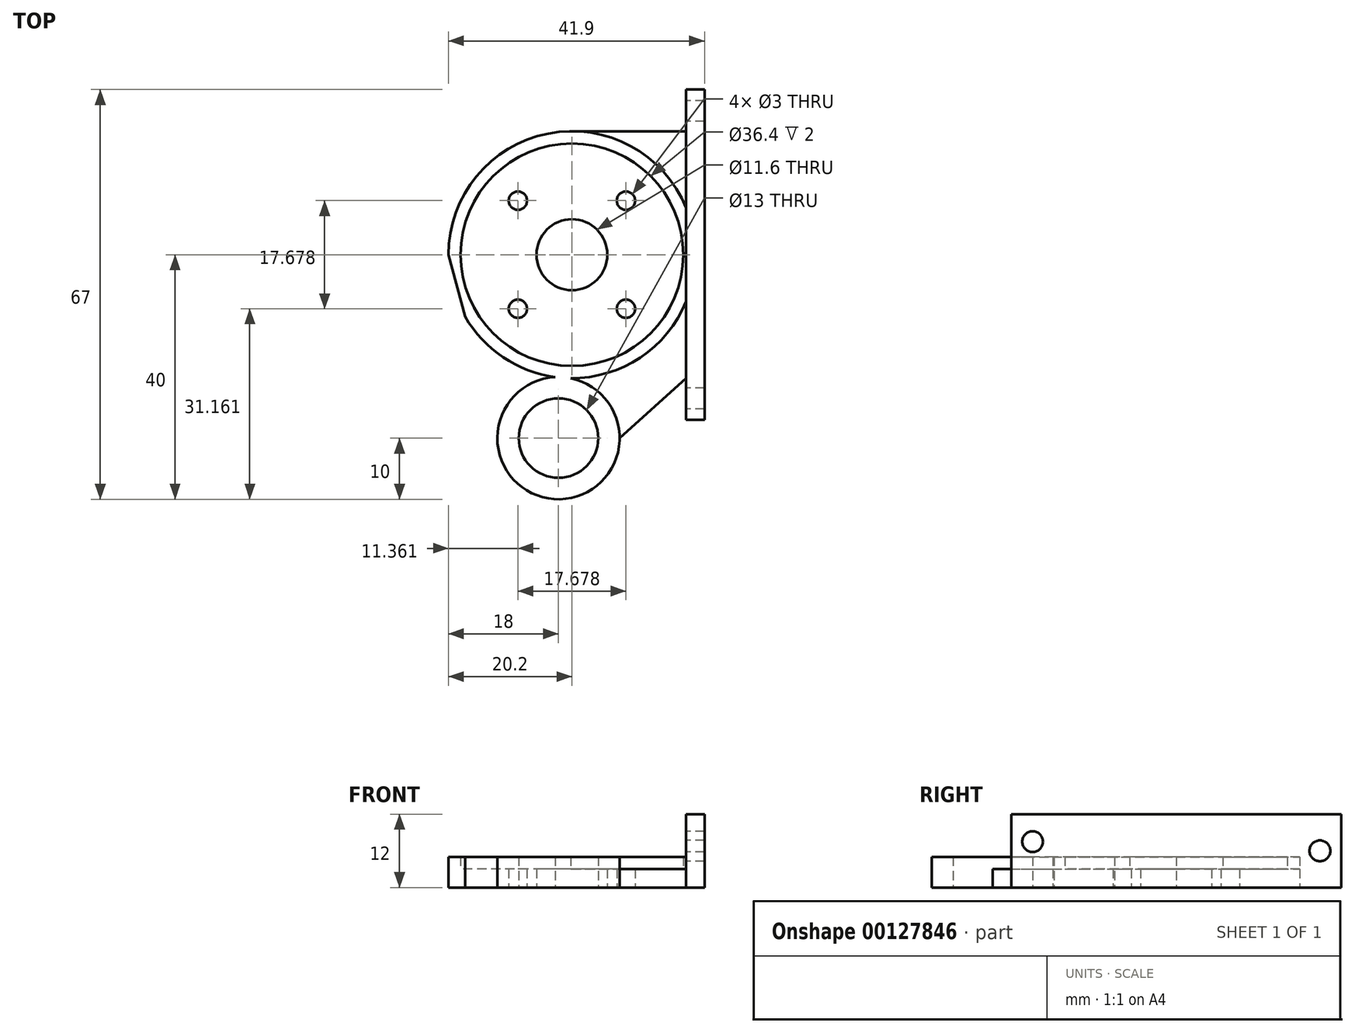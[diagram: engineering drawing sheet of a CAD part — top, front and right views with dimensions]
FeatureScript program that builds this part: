
annotation { "Feature Type Name" : "Feature", "Feature Type Description" : "" }
export const myFeature = defineFeature(function(context is Context, id is Id, definition is map)
    precondition{}
    {
        {
            var Q0;
            Q0=qCreatedBy(makeId("Top.planeOp"),FACE);
            var sketch = newSketch(context, id + "F0", { "sketchPlane" : qUnion([Q0])});
            skCircle(sketch, "E0", {"center": v(0, 0) * mm, "radius": 20.2 * mm});
            skLineSegment(sketch, "E1.bottom", {"start": v(0, 20.2) * mm, "end": v(21.7, 20.2) * mm});
            skLineSegment(sketch, "E1.top", {"start": v(0, -20.2) * mm, "end": v(21.7, -20.2) * mm});
            skLineSegment(sketch, "E1.left", {"start": v(0, 20.2) * mm, "end": v(0, -20.2) * mm});
            skLineSegment(sketch, "E1.right", {"start": v(21.7, 20.2) * mm, "end": v(21.7, -20.2) * mm});
            skLineSegment(sketch, "E2.bottom", {"start": v(21.7, 27) * mm, "end": v(18.7, 27) * mm});
            skLineSegment(sketch, "E2.top", {"start": v(21.7, 0) * mm, "end": v(18.7, 0) * mm});
            skLineSegment(sketch, "E2.left", {"start": v(21.7, 27) * mm, "end": v(21.7, 0) * mm});
            skLineSegment(sketch, "E2.right", {"start": v(18.7, 27) * mm, "end": v(18.7, 0) * mm});
            skLineSegment(sketch, "E3.MirrorCS", {"start": v(21.7, -27) * mm, "end": v(18.7, -27) * mm});
            skLineSegment(sketch, "E4.MirrorCS", {"start": v(18.7, -27) * mm, "end": v(18.7, 0) * mm});
            skLineSegment(sketch, "E5.MirrorCS", {"start": v(21.7, -27) * mm, "end": v(21.7, 0) * mm});
            skCircle(sketch, "E6", {"center": v(0, 0) * mm, "radius": 18.2 * mm});
            skCircle(sketch, "E7.cCircle", {"center": v(0, 0) * mm, "radius": 12.5 * mm, "construction": true});
            skLineSegment(sketch, "E7.0", {"start": v(-8.84, 8.84) * mm, "end": v(8.84, 8.84) * mm});
            skLineSegment(sketch, "E7.1", {"start": v(8.84, 8.84) * mm, "end": v(8.84, -8.84) * mm});
            skLineSegment(sketch, "E7.2", {"start": v(8.84, -8.84) * mm, "end": v(-8.84, -8.84) * mm});
            skLineSegment(sketch, "E7.3", {"start": v(-8.84, -8.84) * mm, "end": v(-8.84, 8.84) * mm});
            skCircle(sketch, "E8", {"center": v(-8.84, -8.84) * mm, "radius": 1.5 * mm});
            skCircle(sketch, "E9", {"center": v(8.84, -8.84) * mm, "radius": 1.5 * mm});
            skCircle(sketch, "E10", {"center": v(8.84, 8.84) * mm, "radius": 1.5 * mm});
            skCircle(sketch, "E11", {"center": v(-8.84, 8.84) * mm, "radius": 1.5 * mm});
            skPoint(sketch, "E12", {"position": v(0, -30) * mm});
            skPoint(sketch, "E13", {"position": v(21.7, -30) * mm});
            skLineSegment(sketch, "E14", {"start": v(21.7, -30) * mm, "end": v(-2.2, -30) * mm});
            skCircle(sketch, "E15", {"center": v(-2.2, -30) * mm, "radius": 6.5 * mm});
            skCircle(sketch, "E16", {"center": v(-2.2, -30) * mm, "radius": 10 * mm});
            skLineSegment(sketch, "E17", {"start": v(-20.2, 0) * mm, "end": v(-12.2, -29.82) * mm});
            skPoint(sketch, "E17.startSnap0", {"position": v(-8.84, 0) * mm});
            skLineSegment(sketch, "E18", {"start": v(7.8, -30) * mm, "end": v(18.7, -20.2) * mm});
            skCircle(sketch, "E19", {"center": v(0, 0) * mm, "radius": 5.8 * mm});
            skSolve(sketch);
        }
        {
            var Q0;
            {var subQ5=sQuery(id+"F0.wireOp",EDGE,"E2.bottom");Q0=makeQuery(id+"F0.imprint","IMPRINT",FACE,{"disambiguationData":[TD([[makeQuery(id+"F0.imprint","IMPRINT",EDGE,{"derivedFrom":subQ5}),1.0]])]});}
            var Q1;
            {var subQ5=sQuery(id+"F0.wireOp",EDGE,"E0");var subQ7=sQuery(id+"F0.wireOp",EDGE,"E2.right");var subQ9=makeQuery(id+"F0.imprint","INTERSECT",VERTEX,{"derivedFrom":[subQ5,subQ7]});Q1=makeQuery(id+"F0.imprint","IMPRINT",FACE,{"disambiguationData":[TD([[makeQuery(id+"F0.imprint","IMPRINT",EDGE,{"disambiguationData":[TD([[subQ9,1.0]])],"derivedFrom":subQ5}),-1.0]])]});}
            var Q2;
            {var subQ3=sQuery(id+"F0.wireOp",EDGE,"E0");var subQ7=sQuery(id+"F0.wireOp",EDGE,"E2.top");var subQ9=makeQuery(id+"F0.imprint","INTERSECT",VERTEX,{"derivedFrom":[subQ3,subQ7]});Q2=makeQuery(id+"F0.imprint","IMPRINT",FACE,{"disambiguationData":[TD([[makeQuery(id+"F0.imprint","IMPRINT",EDGE,{"disambiguationData":[TD([[subQ9,1.0]])],"derivedFrom":subQ3}),-1.0]])]});}
            var Q3;
            {var subQ5=sQuery(id+"F0.wireOp",EDGE,"E3.MirrorCS");Q3=makeQuery(id+"F0.imprint","IMPRINT",FACE,{"disambiguationData":[TD([[makeQuery(id+"F0.imprint","IMPRINT",EDGE,{"derivedFrom":subQ5}),-1.0]])]});}
            var Q4;
            {var subQ0=sQuery(id+"F0.wireOp",EDGE,"E2.right");var subQ1=sQuery(id+"F0.wireOp",EDGE,"E0");var subQ2=makeQuery(id+"F0.imprint","INTERSECT",VERTEX,{"derivedFrom":[subQ1,subQ0]});Q4=makeQuery(id+"F0.imprint","IMPRINT",FACE,{"disambiguationData":[TD([[makeQuery(id+"F0.imprint","IMPRINT",EDGE,{"disambiguationData":[TD([[subQ2,1.0]])],"derivedFrom":subQ1}),1.0]])]});}
            var Q5;
            {var subQ0=sQuery(id+"F0.wireOp",EDGE,"E2.top");var subQ1=sQuery(id+"F0.wireOp",EDGE,"E0");var subQ2=makeQuery(id+"F0.imprint","INTERSECT",VERTEX,{"derivedFrom":[subQ1,subQ0]});Q5=makeQuery(id+"F0.imprint","IMPRINT",FACE,{"disambiguationData":[TD([[makeQuery(id+"F0.imprint","IMPRINT",EDGE,{"disambiguationData":[TD([[subQ2,1.0]])],"derivedFrom":subQ1}),1.0]])]});}
            extrude(context, id + "F1", {"entities" : qUnion([Q0, Q1, Q2, Q3, Q4, Q5]), "depth" : 12 * mm});
        }
        {
            var Q0;
            {var subQ0=sQuery(id+"F0.wireOp",EDGE,"E1.left");var subQ3=sQuery(id+"F0.wireOp",EDGE,"E6");var subQ4=makeQuery(id+"F0.imprint","INTERSECT",VERTEX,{"disambiguationData":[OD(0.0)],"derivedFrom":[subQ0,subQ3]});Q0=makeQuery(id+"F0.imprint","IMPRINT",FACE,{"disambiguationData":[TD([[makeQuery(id+"F0.imprint","IMPRINT",EDGE,{"disambiguationData":[TD([[subQ4,-1.0]])],"derivedFrom":subQ3}),-1.0]])]});}
            var Q1;
            {var subQ0=sQuery(id+"F0.wireOp",EDGE,"E1.left");var subQ3=sQuery(id+"F0.wireOp",EDGE,"E6");var subQ4=makeQuery(id+"F0.imprint","INTERSECT",VERTEX,{"disambiguationData":[OD(0.0)],"derivedFrom":[subQ0,subQ3]});Q1=makeQuery(id+"F0.imprint","IMPRINT",FACE,{"disambiguationData":[TD([[makeQuery(id+"F0.imprint","IMPRINT",EDGE,{"disambiguationData":[TD([[subQ4,1.0]])],"derivedFrom":subQ3}),-1.0]])]});}
            var Q2;
            {var subQ0=sQuery(id+"F0.wireOp",EDGE,"E17");var subQ1=sQuery(id+"F0.wireOp",EDGE,"E0");var subQ2=makeQuery(id+"F0.imprint","INTERSECT",VERTEX,{"disambiguationData":[OD(0.0)],"derivedFrom":[subQ1,subQ0]});Q2=makeQuery(id+"F0.imprint","IMPRINT",FACE,{"disambiguationData":[TD([[makeQuery(id+"F0.imprint","IMPRINT",EDGE,{"disambiguationData":[TD([[subQ2,-1.0]])],"derivedFrom":subQ1}),1.0]])]});}
            extrude(context, id + "F2", {"entities" : qUnion([Q0, Q1, Q2]), "operationType" : NewBodyOperationType.ADD, "depth" : 5 * mm});
        }
        {
            var Q0;
            {var subQ1=sQuery(id+"F0.wireOp",EDGE,"E1.left");var subQ5=sQuery(id+"F0.wireOp",EDGE,"E6");var subQ6=makeQuery(id+"F0.imprint","INTERSECT",VERTEX,{"disambiguationData":[OD(0.0)],"derivedFrom":[subQ1,subQ5]});Q0=makeQuery(id+"F0.imprint","IMPRINT",FACE,{"disambiguationData":[TD([[makeQuery(id+"F0.imprint","IMPRINT",EDGE,{"disambiguationData":[TD([[subQ6,-1.0]])],"derivedFrom":subQ1}),-1.0]])]});}
            var Q1;
            {var subQ6=sQuery(id+"F0.wireOp",EDGE,"E1.left");var subQ9=sQuery(id+"F0.wireOp",EDGE,"E7.0");var subQ10=makeQuery(id+"F0.imprint","INTERSECT",VERTEX,{"derivedFrom":[subQ6,subQ9]});Q1=makeQuery(id+"F0.imprint","IMPRINT",FACE,{"disambiguationData":[TD([[makeQuery(id+"F0.imprint","IMPRINT",EDGE,{"disambiguationData":[TD([[subQ10,-1.0]])],"derivedFrom":subQ6}),1.0]])]});}
            var Q2;
            {var subQ0=sQuery(id+"F0.wireOp",EDGE,"E7.0");var subQ1=sQuery(id+"F0.wireOp",EDGE,"E1.left");var subQ2=makeQuery(id+"F0.imprint","INTERSECT",VERTEX,{"derivedFrom":[subQ1,subQ0]});Q2=makeQuery(id+"F0.imprint","IMPRINT",FACE,{"disambiguationData":[TD([[makeQuery(id+"F0.imprint","IMPRINT",EDGE,{"disambiguationData":[TD([[subQ2,-1.0]])],"derivedFrom":subQ1}),-1.0]])]});}
            var Q3;
            {var subQ1=sQuery(id+"F0.wireOp",EDGE,"E1.left");var subQ7=sQuery(id+"F0.wireOp",EDGE,"E6");var subQ9=makeQuery(id+"F0.imprint","INTERSECT",VERTEX,{"disambiguationData":[OD(0.0)],"derivedFrom":[subQ1,subQ7]});Q3=makeQuery(id+"F0.imprint","IMPRINT",FACE,{"disambiguationData":[TD([[makeQuery(id+"F0.imprint","IMPRINT",EDGE,{"disambiguationData":[TD([[subQ9,-1.0]])],"derivedFrom":subQ1}),1.0]])]});}
            extrude(context, id + "F3", {"entities" : qUnion([Q0, Q1, Q2, Q3]), "operationType" : NewBodyOperationType.ADD, "depth" : 3 * mm});
        }
        {
            var Q0;
            {var subQ0=sQuery(id+"F0.wireOp",EDGE,"E16");var subQ1=sQuery(id+"F0.wireOp",EDGE,"E0");var subQ2=makeQuery(id+"F0.imprint","INTERSECT",VERTEX,{"disambiguationData":[OD(0.0)],"derivedFrom":[subQ1,subQ0]});Q0=makeQuery(id+"F0.imprint","IMPRINT",FACE,{"disambiguationData":[TD([[makeQuery(id+"F0.imprint","IMPRINT",EDGE,{"disambiguationData":[TD([[subQ2,-1.0]])],"derivedFrom":subQ1}),1.0]])]});}
            var Q1;
            Q1=makeQuery(id+"F0.imprint","IMPRINT",FACE,{"disambiguationData":[TD([[makeQuery(id+"F0.imprint","IMPRINT",EDGE,{"derivedFrom":sQuery(id+"F0.wireOp",EDGE,"E15")}),-1.0]])]});
            extrude(context, id + "F4", {"entities" : qUnion([Q0, Q1]), "operationType" : NewBodyOperationType.ADD, "depth" : 5 * mm});
        }
        {
            var Q0;
            {var subQ0=sQuery(id+"F0.wireOp",EDGE,"E17");var subQ1=sQuery(id+"F0.wireOp",EDGE,"E0");var subQ2=makeQuery(id+"F0.imprint","INTERSECT",VERTEX,{"disambiguationData":[OD(1.0)],"derivedFrom":[subQ1,subQ0]});Q0=makeQuery(id+"F0.imprint","IMPRINT",FACE,{"disambiguationData":[TD([[makeQuery(id+"F0.imprint","IMPRINT",EDGE,{"disambiguationData":[TD([[subQ2,-1.0]])],"derivedFrom":subQ1}),-1.0]])]});}
            var Q1;
            {var subQ1=sQuery(id+"F0.wireOp",EDGE,"E0");var subQ3=sQuery(id+"F0.wireOp",EDGE,"E4.MirrorCS");var subQ4=makeQuery(id+"F0.imprint","INTERSECT",VERTEX,{"derivedFrom":[subQ1,subQ3]});Q1=makeQuery(id+"F0.imprint","IMPRINT",FACE,{"disambiguationData":[TD([[makeQuery(id+"F0.imprint","IMPRINT",EDGE,{"disambiguationData":[TD([[subQ4,1.0]])],"derivedFrom":subQ1}),-1.0]])]});}
            var Q2;
            {var subQ5=sQuery(id+"F0.wireOp",EDGE,"E18");Q2=makeQuery(id+"F0.imprint","IMPRINT",FACE,{"disambiguationData":[TD([[makeQuery(id+"F0.imprint","IMPRINT",EDGE,{"derivedFrom":subQ5}),1.0]])]});}
            extrude(context, id + "F5", {"entities" : qUnion([Q0, Q1, Q2]), "operationType" : NewBodyOperationType.ADD, "depth" : 3 * mm});
        }
        {
            var Q0;
            Q0=makeQuery(id+"F1.opExtrude","SWEPT_FACE",FACE,{"disambiguationData":[OSD([sQuery(id+"F0.wireOp",EDGE,"E2.right"),sQuery(id+"F0.wireOp",EDGE,"E4.MirrorCS")])]});
            var sketch = newSketch(context, id + "F6", { "sketchPlane" : qUnion([Q0])});
            skPoint(sketch, "E20", {"position": v(-23.5, 6) * mm});
            skLineSegment(sketch, "E21", {"start": v(-23.5, 6) * mm, "end": v(-27, 6) * mm});
            skLineSegment(sketch, "E22", {"start": v(-23.5, 6) * mm, "end": v(-23.5, 12) * mm});
            skCircle(sketch, "E23", {"center": v(-23.5, 6) * mm, "radius": 1.7 * mm});
            skLineSegment(sketch, "E24", {"start": v(-27, 6) * mm, "end": v(0, 6) * mm});
            skPoint(sketch, "E24.endSnap0", {"position": v(0, 5) * mm});
            skLineSegment(sketch, "E25", {"start": v(0, 6) * mm, "end": v(0, 12) * mm});
            skCircle(sketch, "E26.MirrorC", {"center": v(23.5, 7.5) * mm, "radius": 1.7 * mm});
            skLineSegment(sketch, "E27", {"start": v(23.5, 7.5) * mm, "end": v(23.5, 12) * mm});
            skSolve(sketch);
        }
        {
            var Q0;
            {var subQ0=sQuery(id+"F6.wireOp",EDGE,"E24");var subQ1=sQuery(id+"F6.wireOp",EDGE,"E22");var subQ2=makeQuery(id+"F6.imprint","INTERSECT",VERTEX,{"derivedFrom":[subQ1,subQ0]});Q0=makeQuery(id+"F6.imprint","IMPRINT",FACE,{"disambiguationData":[TD([[makeQuery(id+"F6.imprint","IMPRINT",EDGE,{"disambiguationData":[TD([[subQ2,-1.0]])],"derivedFrom":subQ1}),1.0]])]});}
            var Q1;
            {var subQ0=sQuery(id+"F6.wireOp",EDGE,"E24");var subQ1=sQuery(id+"F6.wireOp",EDGE,"E23");var subQ2=makeQuery(id+"F6.imprint","INTERSECT",VERTEX,{"disambiguationData":[OD(0.0)],"derivedFrom":[subQ1,subQ0]});Q1=makeQuery(id+"F6.imprint","IMPRINT",FACE,{"disambiguationData":[TD([[makeQuery(id+"F6.imprint","IMPRINT",EDGE,{"disambiguationData":[TD([[subQ2,1.0]])],"derivedFrom":subQ1}),1.0]])]});}
            var Q2;
            {var subQ0=sQuery(id+"F6.wireOp",EDGE,"E24");var subQ1=sQuery(id+"F6.wireOp",EDGE,"E22");var subQ2=makeQuery(id+"F6.imprint","INTERSECT",VERTEX,{"derivedFrom":[subQ1,subQ0]});Q2=makeQuery(id+"F6.imprint","IMPRINT",FACE,{"disambiguationData":[TD([[makeQuery(id+"F6.imprint","IMPRINT",EDGE,{"disambiguationData":[TD([[subQ2,-1.0]])],"derivedFrom":subQ1}),-1.0]])]});}
            extrude(context, id + "F7", {"entities" : qUnion([Q0, Q1, Q2]), "operationType" : NewBodyOperationType.REMOVE, "oppositeDirection" : true, "depth" : 25 * mm});
        }
        {
            var Q0;
            Q0 = qSketchRegion(id + "F6", true);
            extrude(context, id + "F8", {"entities" : qUnion([Q0]), "operationType" : NewBodyOperationType.REMOVE, "oppositeDirection" : true, "depth" : 25 * mm});
        }
        {
            var Q0;
            {var subQ0=sQuery(id+"F0.wireOp",EDGE,"E1.bottom");var subQ3=sQuery(id+"F0.wireOp",EDGE,"E2.right");var subQ5=makeQuery(id+"F0.imprint","INTERSECT",VERTEX,{"derivedFrom":[subQ0,subQ3]});Q0=makeQuery(id+"F0.imprint","IMPRINT",FACE,{"disambiguationData":[TD([[makeQuery(id+"F0.imprint","IMPRINT",EDGE,{"disambiguationData":[TD([[subQ5,-1.0]])],"derivedFrom":subQ3}),-1.0]])]});}
            extrude(context, id + "F9", {"entities" : qUnion([Q0]), "operationType" : NewBodyOperationType.ADD, "depth" : 3 * mm});
        }
        {
            var Q0;
            Q0=makeQuery(id+"F1.opExtrude","SWEPT_BODY",BODY,{"disambiguationData":[OSD([sQuery(id+"F0.wireOp",EDGE,"E2.bottom"),sQuery(id+"F0.wireOp",EDGE,"E2.left"),sQuery(id+"F0.wireOp",EDGE,"E2.right"),sQuery(id+"F0.wireOp",EDGE,"E3.MirrorCS"),sQuery(id+"F0.wireOp",EDGE,"E4.MirrorCS"),sQuery(id+"F0.wireOp",EDGE,"E5.MirrorCS")])]});
            transform(context, id + "F10", {"entities" : qUnion([Q0]), "transformType" : TransformType.TRANSLATION_3D, "dx" : 0 * mm, "dy" : 0 * mm, "dz" : 0 * mm, "makeCopy" : true});
        }
        {
            var Q0;
            Q0=makeQuery(id+"F1.opExtrude","SWEPT_BODY",BODY,{"disambiguationData":[OSD([sQuery(id+"F0.wireOp",EDGE,"E2.bottom"),sQuery(id+"F0.wireOp",EDGE,"E2.left"),sQuery(id+"F0.wireOp",EDGE,"E2.right"),sQuery(id+"F0.wireOp",EDGE,"E3.MirrorCS"),sQuery(id+"F0.wireOp",EDGE,"E4.MirrorCS"),sQuery(id+"F0.wireOp",EDGE,"E5.MirrorCS")])]});
            deleteBodies(context, id + "F11", {"entities" : qUnion([Q0])});
        }
    });
